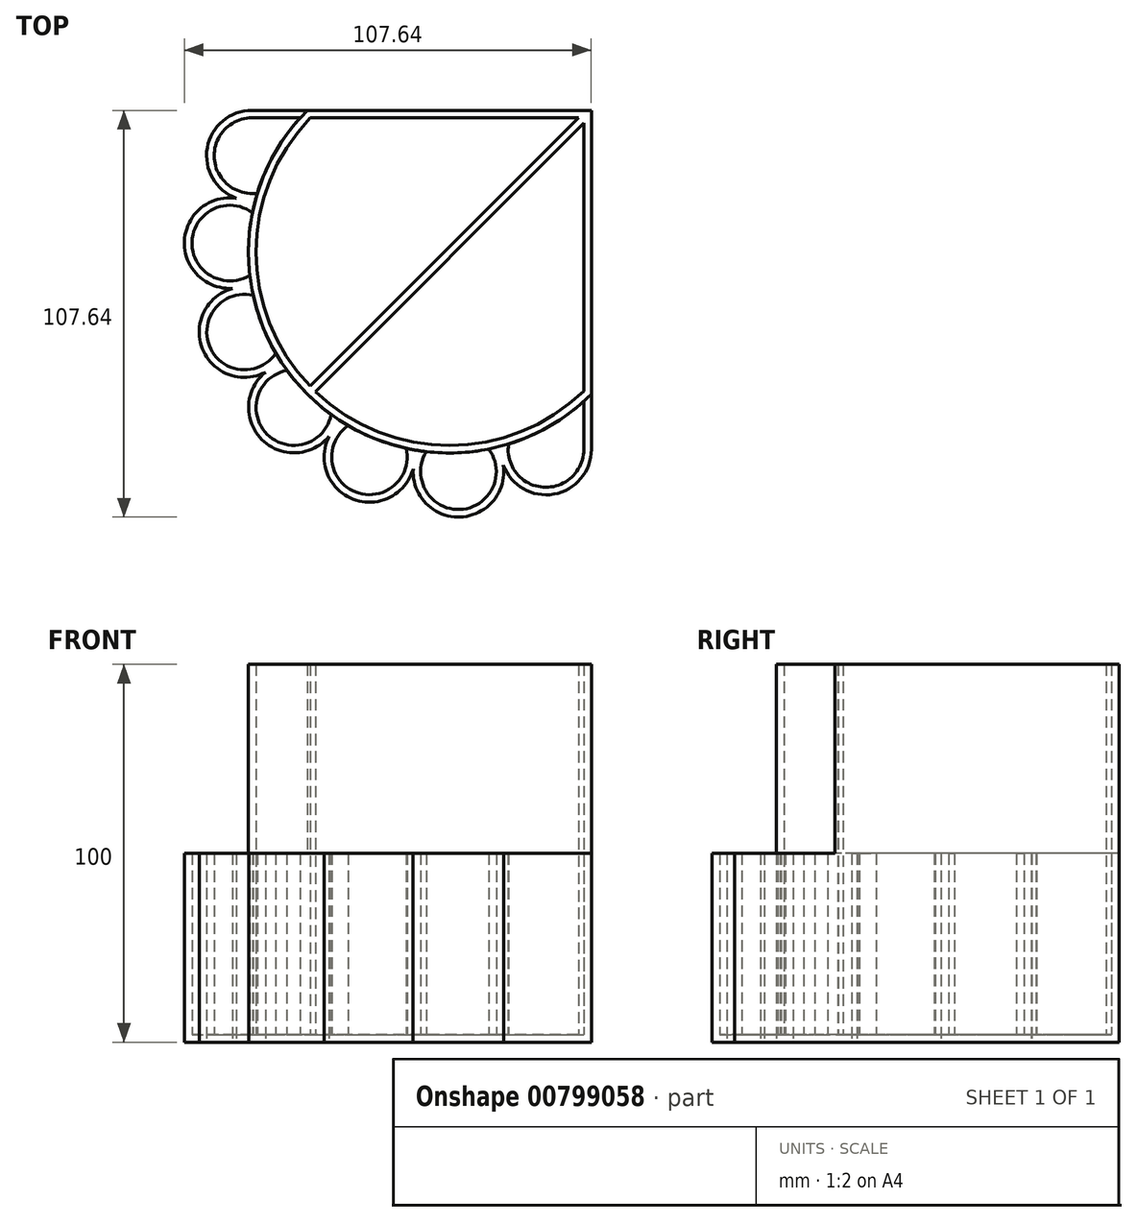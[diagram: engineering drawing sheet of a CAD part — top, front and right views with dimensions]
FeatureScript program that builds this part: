
annotation { "Feature Type Name" : "Feature", "Feature Type Description" : "" }
export const myFeature = defineFeature(function(context is Context, id is Id, definition is map)
    precondition{}
    {
        {
            var Q0;
            Q0=qCreatedBy(makeId("Top.planeOp"),FACE);
            var sketch = newSketch(context, id + "F0", { "sketchPlane" : qUnion([Q0])});
            skLineSegment(sketch, "E0", {"start": v(-53.82, 0) * mm, "end": v(0, 0) * mm, "construction": true});
            skLineSegment(sketch, "E1", {"start": v(0, 0) * mm, "end": v(53.82, 0) * mm, "construction": true});
            skLineSegment(sketch, "E2", {"start": v(0, 53.82) * mm, "end": v(0, 0) * mm, "construction": true});
            skLineSegment(sketch, "E3", {"start": v(0, 0) * mm, "end": v(0, -53.82) * mm, "construction": true});
            skLineSegment(sketch, "E4", {"start": v(-21.31, 53.82) * mm, "end": v(53.82, 53.82) * mm});
            skLineSegment(sketch, "E5", {"start": v(53.82, 53.82) * mm, "end": v(53.82, -21.31) * mm});
            skArc(sketch, "E6", {"start": v(-21.31, 53.82) * mm, "mid": v(-21.31, -21.31) * mm, "end": v(53.82, -21.31) * mm});
            skPoint(sketch, "E6.centerSnap0", {"position": v(53.82, 16.26) * mm});
            skPoint(sketch, "E6.centerSnap1", {"position": v(16.26, 53.82) * mm});
            skLineSegment(sketch, "E7", {"start": v(-21.31, 53.82) * mm, "end": v(-53.82, 53.82) * mm, "construction": true});
            skLineSegment(sketch, "E8", {"start": v(-53.82, 53.82) * mm, "end": v(-53.82, -53.82) * mm, "construction": true});
            skLineSegment(sketch, "E9", {"start": v(-53.82, -53.82) * mm, "end": v(53.82, -53.82) * mm, "construction": true});
            skLineSegment(sketch, "E10", {"start": v(53.82, -53.82) * mm, "end": v(53.82, -21.31) * mm, "construction": true});
            skLineSegment(sketch, "E11", {"start": v(-35.95, 41.82) * mm, "end": v(-31.46, 39.62) * mm, "construction": true});
            skArc(sketch, "E12", {"start": v(-28.1, 53.82) * mm, "mid": v(-24.85, -24.85) * mm, "end": v(53.82, -28.1) * mm, "construction": true});
            skLineSegment(sketch, "E13", {"start": v(-35.95, 41.82) * mm, "end": v(-44.93, 46.22) * mm, "construction": true});
            skLineSegment(sketch, "E14", {"start": v(-44.93, 46.22) * mm, "end": v(-46.73, 47.1) * mm, "construction": true});
            skArc(sketch, "E15", {"start": v(-27.25, 46.75) * mm, "mid": v(-44.93, 46.22) * mm, "end": v(-34.51, 31.93) * mm});
            skArc(sketch, "E16", {"start": v(-40.09, 30.56) * mm, "mid": v(-53.81, 19.19) * mm, "end": v(-41.08, 6.7) * mm});
            skArc(sketch, "E17", {"start": v(-41.08, 6.7) * mm, "mid": v(-49.08, -9.22) * mm, "end": v(-32.41, -15.53) * mm});
            skArc(sketch, "E18", {"start": v(-32.41, -15.53) * mm, "mid": v(-33.33, -33.33) * mm, "end": v(-15.53, -32.41) * mm});
            skLineSegment(sketch, "E19", {"start": v(-29.64, -10.5) * mm, "end": v(-29.64, -10.5) * mm});
            skArc(sketch, "E20", {"start": v(-26.7, -15.02) * mm, "mid": v(-31.92, -31.92) * mm, "end": v(-15.02, -26.7) * mm});
            skArc(sketch, "E21", {"start": v(-15.53, -32.41) * mm, "mid": v(-9.22, -49.08) * mm, "end": v(6.7, -41.08) * mm});
            skArc(sketch, "E22", {"start": v(-10.5, -29.64) * mm, "mid": v(-8.5, -47.22) * mm, "end": v(4.88, -35.64) * mm});
            skArc(sketch, "E23", {"start": v(-40.09, 30.56) * mm, "mid": v(-46.73, 47.1) * mm, "end": v(-29.59, 52) * mm});
            skLineSegment(sketch, "E24", {"start": v(-35.95, 53.82) * mm, "end": v(-21.31, 53.82) * mm});
            skArc(sketch, "E25", {"start": v(-35.64, 4.88) * mm, "mid": v(-47.22, -8.5) * mm, "end": v(-29.64, -10.5) * mm});
            skArc(sketch, "E26", {"start": v(-35.84, 26.7) * mm, "mid": v(-51.81, 19.1) * mm, "end": v(-36.53, 10.2) * mm});
            skArc(sketch, "E27", {"start": v(6.7, -41.08) * mm, "mid": v(19.19, -53.81) * mm, "end": v(30.56, -40.09) * mm});
            skArc(sketch, "E28", {"start": v(30.56, -40.09) * mm, "mid": v(47.1, -46.73) * mm, "end": v(52, -29.59) * mm});
            skArc(sketch, "E29", {"start": v(10.2, -36.53) * mm, "mid": v(19.1, -51.81) * mm, "end": v(26.7, -35.84) * mm});
            skArc(sketch, "E30", {"start": v(31.93, -34.51) * mm, "mid": v(46.22, -44.93) * mm, "end": v(46.75, -27.25) * mm});
            skLineSegment(sketch, "E31", {"start": v(53.82, -35.95) * mm, "end": v(53.82, -21.31) * mm});
            skLineSegment(sketch, "E32", {"start": v(-39.56, 32.5) * mm, "end": v(-30.8, 50.4) * mm, "construction": true});
            skLineSegment(sketch, "E33", {"start": v(53.82, -35.95) * mm, "end": v(51.82, -35.95) * mm, "construction": true});
            skLineSegment(sketch, "E34", {"start": v(-35.95, 53.82) * mm, "end": v(-35.95, 51.82) * mm, "construction": true});
            skLineSegment(sketch, "E35", {"start": v(-35.95, 51.82) * mm, "end": v(-23.21, 51.82) * mm});
            skLineSegment(sketch, "E36", {"start": v(51.82, -35.95) * mm, "end": v(51.82, -23.21) * mm});
            skLineSegment(sketch, "E37", {"start": v(51.82, 51.82) * mm, "end": v(-20.48, 51.82) * mm});
            skLineSegment(sketch, "E38", {"start": v(51.82, 51.82) * mm, "end": v(51.82, -20.48) * mm});
            skArc(sketch, "E39", {"start": v(-20.48, 51.82) * mm, "mid": v(-19.9, -19.9) * mm, "end": v(51.82, -20.48) * mm});
            skLineSegment(sketch, "E40", {"start": v(-31.46, 39.62) * mm, "end": v(-29.66, 38.74) * mm, "construction": true});
            skLineSegment(sketch, "E41", {"start": v(51.82, 51.82) * mm, "end": v(16.26, 16.26) * mm, "construction": true});
            skLineSegment(sketch, "E42", {"start": v(16.26, 16.26) * mm, "end": v(-19.9, -19.9) * mm, "construction": true});
            skLineSegment(sketch, "E43", {"start": v(-20.6, -19.18) * mm, "end": v(50.4, 51.82) * mm});
            skLineSegment(sketch, "E44", {"start": v(-19.18, -20.6) * mm, "end": v(51.82, 50.4) * mm});
            skLineSegment(sketch, "E45", {"start": v(16.26, 16.26) * mm, "end": v(15.55, 16.96) * mm, "construction": true});
            skLineSegment(sketch, "E46", {"start": v(16.26, 16.26) * mm, "end": v(16.96, 15.55) * mm, "construction": true});
            skLineSegment(sketch, "E47", {"start": v(-0.7, 0.7) * mm, "end": v(0.7, -0.7) * mm, "construction": true});
            skSolve(sketch);
        }
        {
            var Q0;
            {var subQ12=sQuery(id+"F0.wireOp",EDGE,"E4");Q0=makeQuery(id+"F0.imprint","IMPRINT",FACE,{"disambiguationData":[TD([[makeQuery(id+"F0.imprint","IMPRINT",EDGE,{"derivedFrom":subQ12}),-1.0]])]});}
            var Q1;
            {var subQ0=sQuery(id+"F0.wireOp",EDGE,"E43");Q1=makeQuery(id+"F0.imprint","IMPRINT",FACE,{"disambiguationData":[TD([[makeQuery(id+"F0.imprint","IMPRINT",EDGE,{"derivedFrom":subQ0}),-1.0]])]});}
            extrude(context, id + "F1", {"entities" : qUnion([Q0, Q1]), "depth" : 100 * mm, "offsetDistance" : 25 * mm});
        }
        {
            var Q0;
            {var subQ4=sQuery(id+"F0.wireOp",EDGE,"E16");Q0=makeQuery(id+"F0.imprint","IMPRINT",FACE,{"disambiguationData":[TD([[makeQuery(id+"F0.imprint","IMPRINT",EDGE,{"derivedFrom":subQ4}),1.0]])]});}
            var Q1;
            {var subQ0=sQuery(id+"F0.wireOp",EDGE,"E31");Q1=makeQuery(id+"F0.imprint","IMPRINT",FACE,{"disambiguationData":[TD([[makeQuery(id+"F0.imprint","IMPRINT",EDGE,{"derivedFrom":subQ0}),1.0]])]});}
            var Q2;
            {var subQ0=sQuery(id+"F0.wireOp",EDGE,"E24");Q2=makeQuery(id+"F0.imprint","IMPRINT",FACE,{"disambiguationData":[TD([[makeQuery(id+"F0.imprint","IMPRINT",EDGE,{"derivedFrom":subQ0}),-1.0]])]});}
            extrude(context, id + "F2", {"entities" : qUnion([Q0, Q1, Q2]), "operationType" : NewBodyOperationType.ADD, "depth" : 50 * mm, "offsetDistance" : 25 * mm});
        }
        {
            var Q0;
            {var subQ0=sQuery(id+"F0.wireOp",EDGE,"E25");Q0=makeQuery(id+"F0.imprint","IMPRINT",FACE,{"disambiguationData":[TD([[makeQuery(id+"F0.imprint","IMPRINT",EDGE,{"derivedFrom":subQ0}),1.0]])]});}
            var Q1;
            {var subQ0=sQuery(id+"F0.wireOp",EDGE,"E20");Q1=makeQuery(id+"F0.imprint","IMPRINT",FACE,{"disambiguationData":[TD([[makeQuery(id+"F0.imprint","IMPRINT",EDGE,{"derivedFrom":subQ0}),1.0]])]});}
            var Q2;
            {var subQ0=sQuery(id+"F0.wireOp",EDGE,"E22");Q2=makeQuery(id+"F0.imprint","IMPRINT",FACE,{"disambiguationData":[TD([[makeQuery(id+"F0.imprint","IMPRINT",EDGE,{"derivedFrom":subQ0}),1.0]])]});}
            var Q3;
            {var subQ0=sQuery(id+"F0.wireOp",EDGE,"E29");Q3=makeQuery(id+"F0.imprint","IMPRINT",FACE,{"disambiguationData":[TD([[makeQuery(id+"F0.imprint","IMPRINT",EDGE,{"derivedFrom":subQ0}),1.0]])]});}
            var Q4;
            {var subQ0=sQuery(id+"F0.wireOp",EDGE,"E30");var subQ1=sQuery(id+"F0.wireOp",EDGE,"E6");var subQ2=makeQuery(id+"F0.imprint","INTERSECT",VERTEX,{"disambiguationData":[OD(0.0)],"derivedFrom":[subQ1,subQ0]});Q4=makeQuery(id+"F0.imprint","IMPRINT",FACE,{"disambiguationData":[TD([[makeQuery(id+"F0.imprint","IMPRINT",EDGE,{"disambiguationData":[TD([[subQ2,-1.0]])],"derivedFrom":subQ1}),-1.0]])]});}
            var Q5;
            Q5=makeQuery(id+"F0.imprint","IMPRINT",FACE,{"disambiguationData":[TD([[makeQuery(id+"F0.imprint","IMPRINT",EDGE,{"derivedFrom":sQuery(id+"F0.wireOp",EDGE,"E37")}),1.0]])]});
            var Q6;
            {var subQ0=sQuery(id+"F0.wireOp",EDGE,"E26");Q6=makeQuery(id+"F0.imprint","IMPRINT",FACE,{"disambiguationData":[TD([[makeQuery(id+"F0.imprint","IMPRINT",EDGE,{"derivedFrom":subQ0}),1.0]])]});}
            var Q7;
            {var subQ0=sQuery(id+"F0.wireOp",EDGE,"E15");var subQ1=sQuery(id+"F0.wireOp",EDGE,"E6");var subQ2=makeQuery(id+"F0.imprint","INTERSECT",VERTEX,{"disambiguationData":[OD(0.0)],"derivedFrom":[subQ1,subQ0]});Q7=makeQuery(id+"F0.imprint","IMPRINT",FACE,{"disambiguationData":[TD([[makeQuery(id+"F0.imprint","IMPRINT",EDGE,{"disambiguationData":[TD([[subQ2,-1.0]])],"derivedFrom":subQ1}),-1.0]])]});}
            var Q8;
            {var subQ3=sQuery(id+"F0.wireOp",EDGE,"E36");Q8=makeQuery(id+"F0.imprint","IMPRINT",FACE,{"disambiguationData":[TD([[makeQuery(id+"F0.imprint","IMPRINT",EDGE,{"derivedFrom":subQ3}),1.0]])]});}
            var Q9;
            {var subQ3=sQuery(id+"F0.wireOp",EDGE,"E35");Q9=makeQuery(id+"F0.imprint","IMPRINT",FACE,{"disambiguationData":[TD([[makeQuery(id+"F0.imprint","IMPRINT",EDGE,{"derivedFrom":subQ3}),-1.0]])]});}
            var Q10;
            {var subQ3=sQuery(id+"F0.wireOp",EDGE,"E44");Q10=makeQuery(id+"F0.imprint","IMPRINT",FACE,{"disambiguationData":[TD([[makeQuery(id+"F0.imprint","IMPRINT",EDGE,{"derivedFrom":subQ3}),-1.0]])]});}
            extrude(context, id + "F3", {"entities" : qUnion([Q0, Q1, Q2, Q3, Q4, Q5, Q6, Q7, Q8, Q9, Q10]), "operationType" : NewBodyOperationType.ADD, "depth" : 2 * mm, "offsetDistance" : 25 * mm});
        }
    });
